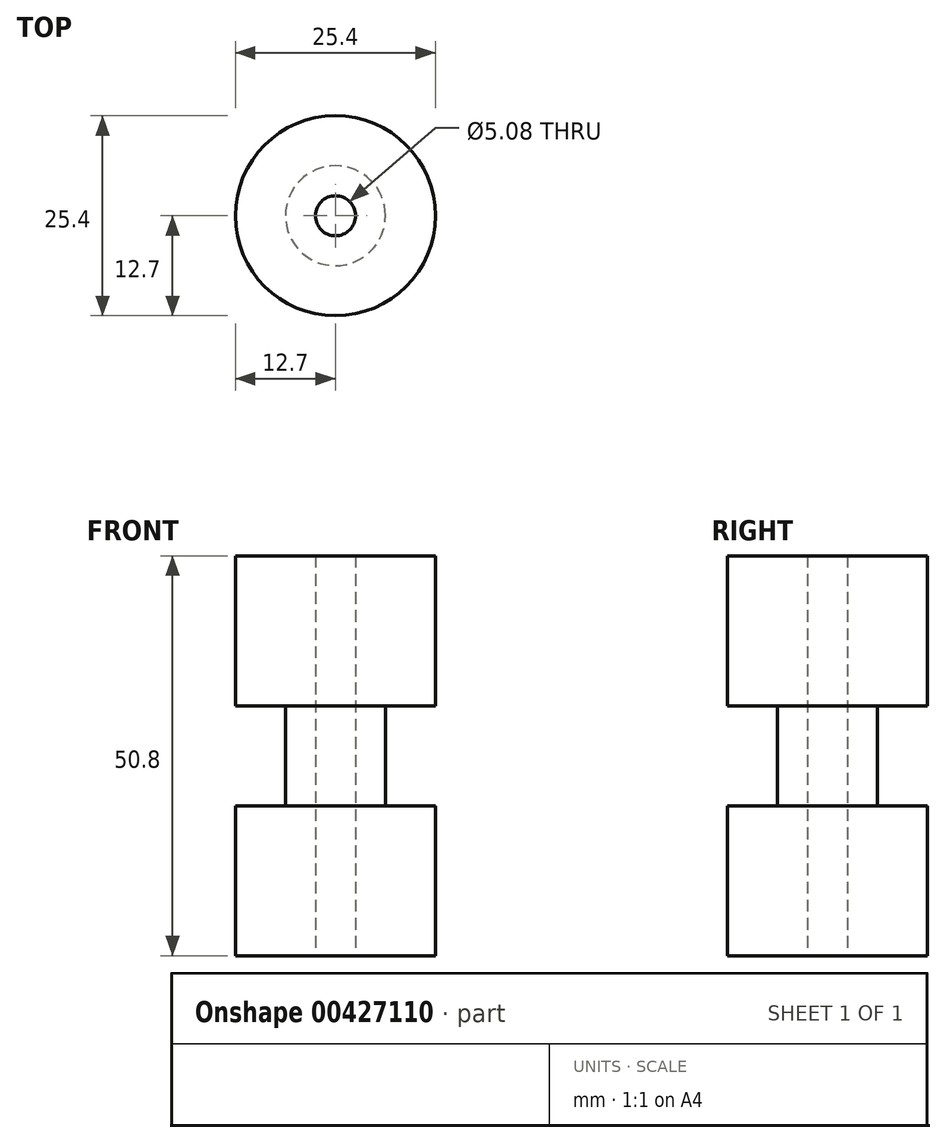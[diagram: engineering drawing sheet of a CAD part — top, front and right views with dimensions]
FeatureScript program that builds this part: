
annotation { "Feature Type Name" : "Feature", "Feature Type Description" : "" }
export const myFeature = defineFeature(function(context is Context, id is Id, definition is map)
    precondition{}
    {
        {
            var Q0;
            Q0=qCreatedBy(makeId("Top.planeOp"),FACE);
            var sketch = newSketch(context, id + "F0", { "sketchPlane" : qUnion([Q0])});
            skCircle(sketch, "E0", {"center": v(0, 0) * mm, "radius": 12.7 * mm});
            skSolve(sketch);
        }
        {
            var Q0;
            Q0 = qSketchRegion(id + "F0", true);
            extrude(context, id + "F1", {"entities" : qUnion([Q0]), "depth" : 19.05 * mm});
        }
        {
            var Q0;
            Q0=makeQuery(id+"F1.opExtrude","CAP_FACE",FACE,{"disambiguationData":[OSD([sQuery(id+"F0.wireOp",EDGE,"E0")])],"isStart":false});
            var sketch = newSketch(context, id + "F2", { "sketchPlane" : qUnion([Q0])});
            skCircle(sketch, "E1", {"center": v(0, 0) * mm, "radius": 6.35 * mm});
            skSolve(sketch);
        }
        {
            var Q0;
            Q0 = qSketchRegion(id + "F2", true);
            extrude(context, id + "F3", {"entities" : qUnion([Q0]), "operationType" : NewBodyOperationType.ADD, "depth" : 12.7 * mm});
        }
        {
            var Q0;
            Q0=makeQuery(id+"F3.opExtrude","CAP_FACE",FACE,{"disambiguationData":[OSD([sQuery(id+"F2.wireOp",EDGE,"E1")])],"isStart":false});
            var sketch = newSketch(context, id + "F4", { "sketchPlane" : qUnion([Q0])});
            skCircle(sketch, "E2", {"center": v(0, 0) * mm, "radius": 12.7 * mm});
            skSolve(sketch);
        }
        {
            var Q0;
            Q0 = qSketchRegion(id + "F4", true);
            extrude(context, id + "F5", {"entities" : qUnion([Q0]), "operationType" : NewBodyOperationType.ADD, "depth" : 19.05 * mm});
        }
        {
            var Q0;
            Q0=makeQuery(id+"F1.opExtrude","CAP_FACE",FACE,{"disambiguationData":[OSD([sQuery(id+"F0.wireOp",EDGE,"E0")])],"isStart":true});
            var sketch = newSketch(context, id + "F6", { "sketchPlane" : qUnion([Q0])});
            skCircle(sketch, "E3", {"center": v(0, 0) * mm, "radius": 2.54 * mm});
            skSolve(sketch);
        }
        {
            var Q0;
            Q0 = qSketchRegion(id + "F6", true);
            extrude(context, id + "F7", {"entities" : qUnion([Q0]), "operationType" : NewBodyOperationType.REMOVE, "oppositeDirection" : true, "depth" : 50.8 * mm});
        }
    });
